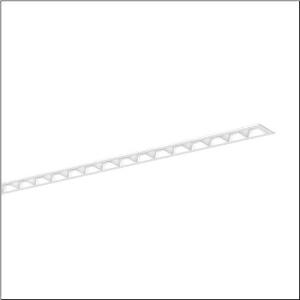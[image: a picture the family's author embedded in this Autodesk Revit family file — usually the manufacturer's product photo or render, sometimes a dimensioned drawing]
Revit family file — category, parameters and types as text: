
# Revit family: silica_r__21_51mx16dc4awb_037f
name_source: partatom
category: Lighting Fixtures
units: mm (PartAtom-declared; Revit-internal decimal feet)

## family parameters
Cut with Voids When Loaded = No
Host = Face
Light Source = No
Part Type = Normal
Room Calculation Point = No
Round Connector Dimension = Use Diameter
Shared = No

## types (1)
- --- (1 x LED, 10800 lm, 60.6 W, 4000K)
    Apparent Load = 61 VA
    CIE Flux Codes = 83 98 100 100 100
    Color Rendering = 80
    Color Temperature = 4000K
    Default Elevation = 1800 mm
    Description = Silica® 21, office luminaire, primary light control with darklight reflector, of PMMA, white, CAT 2 (L<= 3000cd/m²), light emission: direct distribution, primary light characteristic: symmetric, installation type: recessed, LED, rated luminous flux: 10.800lm, luminous efficacy: 178lm/W, light colour: 840, colour temperature: 4000K, with terminal, 3+2-pole, max. 2.5mm², mains connection: 220..240V, AC, 50/60Hz, rated input power: 60.6W, luminaire housing, of aluminium, traffic white (RAL 9016), length: 3.028mm, width: 79mm, height: 53mm, protection rating (complete): IP20, insulation class (complete): insulation class I (protective earthing), certification: CE, permissible operating ambient temperature: 0..+35°C, standard: EN 50419, packaging unit: 1 piece
    Height = 0 mm  [stored 0 ft]
    Lamp = 1 x LED
    Lamp Light Flux = 10800 lm
    Lamp Power = 60.6 W
    Lamp count = 1
    Length = 3027 mm
    Luminous efficacy = 178 lm/W
    Manufacturer = Siteco
    ModVariant = No
    Model = 51MX16DC4AWB
    Mounting Place = Ceiling
    Mounting Type = Recessed
    Number of Poles = 1
    OnlyDefault = Yes
    Power Factor = 1
    Product Name = Silica® 21
    Product group = office luminaire | ceiling recessed
    ProductGroupID = 401
    Protection Class = Protection class I
    Protection Degree = IP 20
    RLX_Detail_Level = 1
    RLX_Emergency_Light_Flux = 0 lm
    RLX_Emergency_Type = 0
    RLX_Emergency_Type_DB = No
    RlxData = <blob elided: 59901 chars, md5=44e42ac3>
    Socket = socket
    Standby Power = 0 W
    System Light Flux = 10800 lm
    System Power = 61 W
    Type Comments = factory setting: luminous flux: 100 % | dim-lin: 254 | 336 mA
    Type Image = l_1313606.jpg
    URL = http://relux.com
    VarID = @adj_073231
    Voltage = 0 V
    Weight = 0.00 kg
    Width = 79 mm

note: [stored X ft] marks values corroborated as IEEE doubles in the binary element streams (Revit-internal decimal feet)

## geometry (parser evidence)
native form markers: Blend x4, Sweep x11
no freeform markers — native parametric forms only
